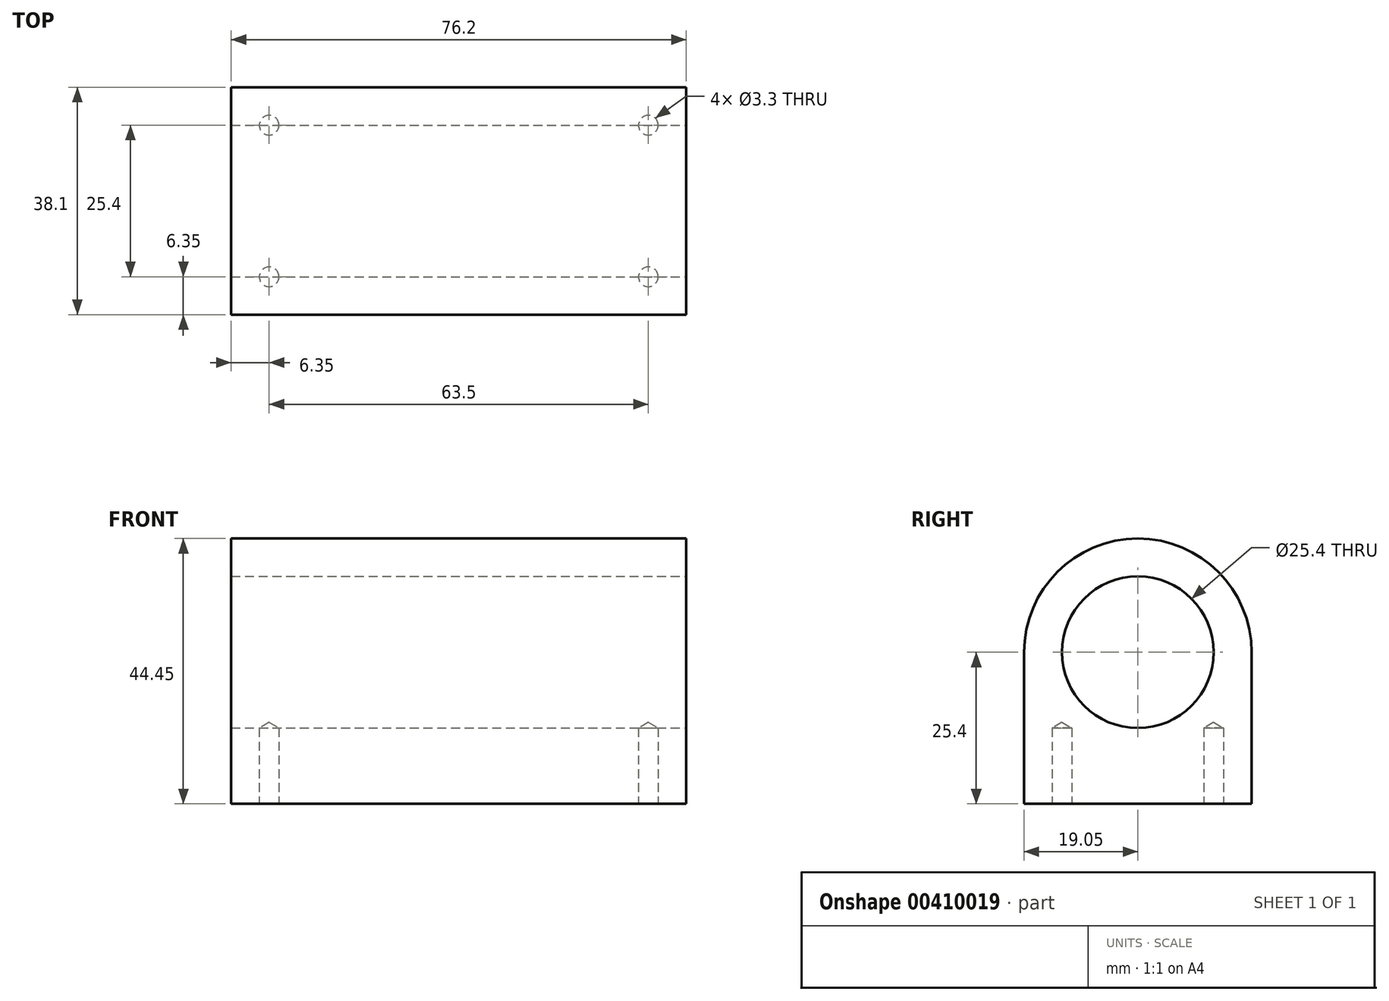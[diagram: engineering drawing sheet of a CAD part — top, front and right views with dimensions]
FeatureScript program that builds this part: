
annotation { "Feature Type Name" : "Feature", "Feature Type Description" : "" }
export const myFeature = defineFeature(function(context is Context, id is Id, definition is map)
    precondition{}
    {
        {
            var Q0;
            Q0=qCreatedBy(makeId("Right.planeOp"),FACE);
            var sketch = newSketch(context, id + "F0", { "sketchPlane" : qUnion([Q0])});
            skArc(sketch, "E0", {"start": v(19.05, 0) * mm, "mid": v(0, 19.05) * mm, "end": v(-19.05, 0) * mm});
            skCircle(sketch, "E1", {"center": v(0, 0) * mm, "radius": 12.7 * mm});
            skLineSegment(sketch, "E2", {"start": v(-19.05, 0) * mm, "end": v(-19.05, -25.4) * mm});
            skLineSegment(sketch, "E3", {"start": v(19.05, 0) * mm, "end": v(19.05, -25.4) * mm});
            skLineSegment(sketch, "E4", {"start": v(-19.05, -25.4) * mm, "end": v(19.05, -25.4) * mm});
            skSolve(sketch);
        }
        {
            var Q0;
            Q0=makeQuery(id+"F0.imprint","IMPRINT",FACE,{"disambiguationData":[TD([[makeQuery(id+"F0.imprint","IMPRINT",EDGE,{"derivedFrom":sQuery(id+"F0.wireOp",EDGE,"E0")}),1.0]])]});
            extrude(context, id + "F1", {"entities" : qUnion([Q0]), "oppositeDirection" : true, "depth" : 76.2 * mm});
        }
        {
            var Q0;
            Q0=makeQuery(id+"F1.opExtrude","SWEPT_FACE",FACE,{"disambiguationData":[OSD([sQuery(id+"F0.wireOp",EDGE,"E4")])]});
            var sketch = newSketch(context, id + "F2", { "sketchPlane" : qUnion([Q0])});
            skCircle(sketch, "E5", {"center": v(-69.85, 12.7) * mm, "radius": 1.65 * mm});
            skCircle(sketch, "E6", {"center": v(-6.35, 12.7) * mm, "radius": 1.65 * mm});
            skCircle(sketch, "E7", {"center": v(-6.35, -12.7) * mm, "radius": 1.65 * mm});
            skCircle(sketch, "E8", {"center": v(-69.85, -12.7) * mm, "radius": 1.65 * mm});
            skSolve(sketch);
        }
        {
            var Q0;
            Q0=sQuery(id+"F2.wireOp",VERTEX,"E5.center");
            var Q1;
            Q1=sQuery(id+"F2.wireOp",VERTEX,"E8.center");
            var Q2;
            Q2=sQuery(id+"F2.wireOp",VERTEX,"E7.center");
            var Q3;
            Q3=sQuery(id+"F2.wireOp",VERTEX,"E6.center");
            var Q4;
            Q4=makeQuery(id+"F1.opExtrude","SWEPT_BODY",BODY,{"disambiguationData":[OSD([sQuery(id+"F0.wireOp",EDGE,"E0"),sQuery(id+"F0.wireOp",EDGE,"E1"),sQuery(id+"F0.wireOp",EDGE,"E2"),sQuery(id+"F0.wireOp",EDGE,"E3"),sQuery(id+"F0.wireOp",EDGE,"E4")])]});
            hole(context, id + "F3", {"style" : HoleStyle.SIMPLE, "endStyle" : HoleEndStyle.BLIND, "holeDiameter" : 3.3 * mm, "holeDepth" : 12.7 * mm, "isTappedThrough" : true, "tappedDepth" : 12.7 * mm, "tapClearance" : 3, "locations" : qUnion([Q0, Q1, Q2, Q3]), "scope" : qUnion([Q4])});
        }
    });
